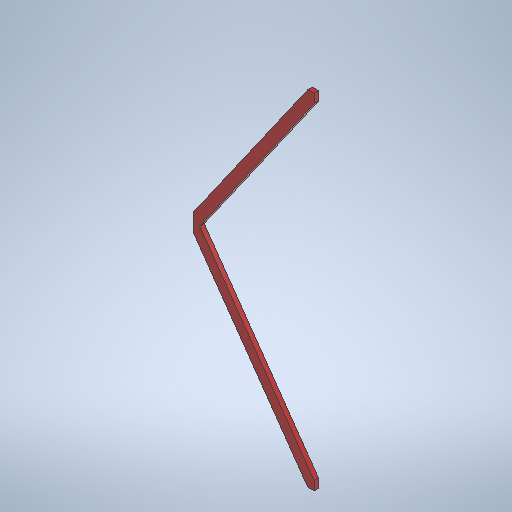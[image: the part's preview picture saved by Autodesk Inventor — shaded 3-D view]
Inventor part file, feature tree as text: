
AUTODESK INVENTOR PART (.ipt)
format: ipt  version: 2025.1 (Build 291241020, 241B)  size: 264,192 bytes
history: native  units: in
note: dims shown in document units (in); Inventor stores cm internally (conversion verified against a paired STEP export)
features: other x7, reference x4, extrude x1, sketch x1
ambient origin geometry x8: Origin, YZ Plane, XZ Plane, XY Plane, X Axis, Y Axis, Z Axis, Center Point
bodies: Solid1 (feature_tree)
feature tree (13):
  extrude  "Extrusion1"  [1 undecoded]
  sketch  "Sketch1"  dims[d4=1.5in d5=0.0in]
  reference  "Reference1"
  reference  "Reference2"
  reference  "Reference3"
  reference  "Reference4"
  other  "<userpath>\Documents\Tburn24\F_Legs1\B_Legs0.iam"
  other  "B_Legs0.iam"
  other  "8'x2x4:3"
  other  "3'5x2x4:3"
  other  "8'x2x4:4"
  other  "3'5x2x4:2"
  other  "Finish1"
note: 1 required parameter value undecoded (feature->parameter linkage not recoverable at this tier; creation-order binding heuristic only, values carry confidence <= 0.55)
